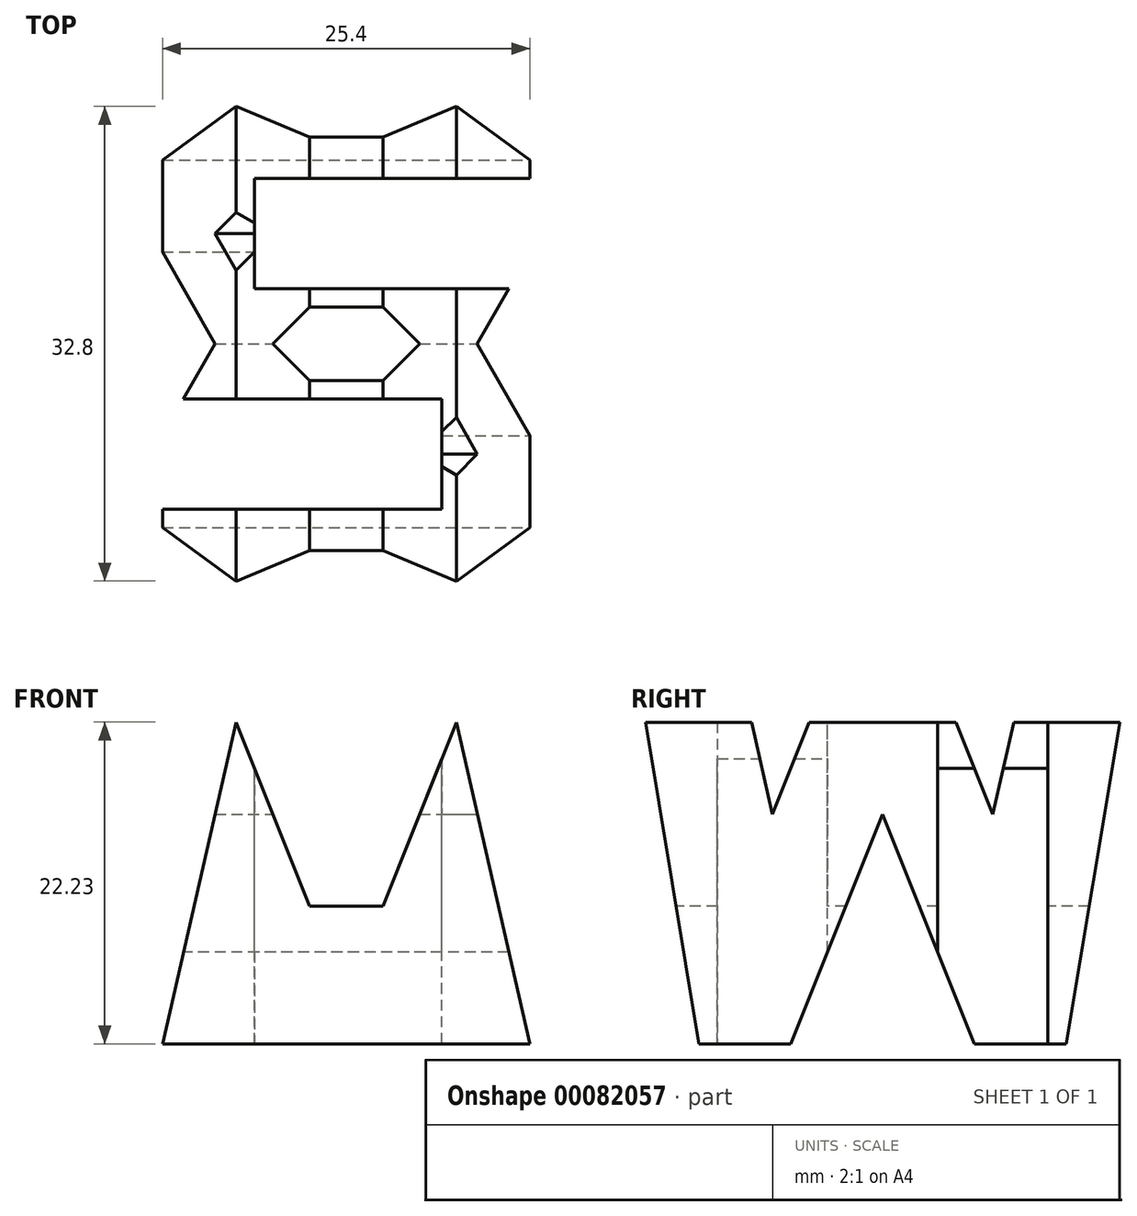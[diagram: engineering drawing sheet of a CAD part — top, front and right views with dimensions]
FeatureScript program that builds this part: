
annotation { "Feature Type Name" : "Feature", "Feature Type Description" : "" }
export const myFeature = defineFeature(function(context is Context, id is Id, definition is map)
    precondition{}
    {
        {
            var Q0;
            Q0=qCreatedBy(makeId("Front.planeOp"),FACE);
            var sketch = newSketch(context, id + "F0", { "sketchPlane" : qUnion([Q0])});
            skLineSegment(sketch, "E0", {"start": v(0, 0) * mm, "end": v(0, 38.1) * mm});
            skLineSegment(sketch, "E1", {"start": v(0, 38.1) * mm, "end": v(38.1, 38.1) * mm});
            skLineSegment(sketch, "E2", {"start": v(38.1, 38.1) * mm, "end": v(38.1, 0) * mm});
            skLineSegment(sketch, "E3", {"start": v(38.1, 0) * mm, "end": v(0, 0) * mm});
            skSolve(sketch);
        }
        {
            var Q0;
            Q0=makeQuery(id+"F0.imprint","IMPRINT",FACE,{"disambiguationData":[TD([[makeQuery(id+"F0.imprint","IMPRINT",EDGE,{"derivedFrom":sQuery(id+"F0.wireOp",EDGE,"E0")}),-1.0]])]});
            extrude(context, id + "F1", {"entities" : qUnion([Q0]), "depth" : 38.1 * mm});
        }
        {
            var Q0;
            Q0=qCreatedBy(makeId("Front.planeOp"),FACE);
            cPlane(context, id + "F2", {"entities" : qUnion([Q0]), "cplaneType" : CPlaneType.OFFSET, "offset" : 38.1 * mm, "width" : 152.4 * mm, "height" : 152.4 * mm});
        }
        {
            var Q0;
            Q0=qCreatedBy(makeId("Right.planeOp"),FACE);
            cPlane(context, id + "F3", {"entities" : qUnion([Q0]), "cplaneType" : CPlaneType.OFFSET, "offset" : 38.1 * mm, "width" : 152.4 * mm, "height" : 152.4 * mm});
        }
        {
            var Q0;
            Q0=qCreatedBy(makeId("Top.planeOp"),FACE);
            cPlane(context, id + "F4", {"entities" : qUnion([Q0]), "cplaneType" : CPlaneType.OFFSET, "offset" : 38.1 * mm, "width" : 152.4 * mm, "height" : 152.4 * mm});
        }
        {
            var Q0;
            Q0=qCreatedBy(id+"F3.planeOp",FACE);
            var sketch = newSketch(context, id + "F5", { "sketchPlane" : qUnion([Q0])});
            skLineSegment(sketch, "E4", {"start": v(0, 0) * mm, "end": v(0, 38.1) * mm});
            skLineSegment(sketch, "E5", {"start": v(0, 38.1) * mm, "end": v(-38.1, 38.1) * mm});
            skLineSegment(sketch, "E6", {"start": v(-38.1, 38.1) * mm, "end": v(-38.1, 0) * mm});
            skLineSegment(sketch, "E7", {"start": v(-38.1, 0) * mm, "end": v(0, 0) * mm});
            skLineSegment(sketch, "E8", {"start": v(-38.1, 38.1) * mm, "end": v(-31.75, 0) * mm});
            skLineSegment(sketch, "E9", {"start": v(-6.35, 0) * mm, "end": v(0, 38.1) * mm});
            skLineSegment(sketch, "E10", {"start": v(-6.35, 38.1) * mm, "end": v(-11.43, 15.87) * mm});
            skLineSegment(sketch, "E11", {"start": v(-16.5, 28.58) * mm, "end": v(-21.59, 28.58) * mm});
            skLineSegment(sketch, "E12", {"start": v(-21.59, 28.58) * mm, "end": v(-26.67, 15.87) * mm});
            skLineSegment(sketch, "E13", {"start": v(-26.67, 15.88) * mm, "end": v(-31.75, 38.1) * mm});
            skLineSegment(sketch, "E14", {"start": v(-16.5, 28.58) * mm, "end": v(-11.43, 15.88) * mm});
            skLineSegment(sketch, "E15", {"start": v(-25.4, 0) * mm, "end": v(-19.05, 15.88) * mm});
            skLineSegment(sketch, "E16", {"start": v(-19.05, 15.88) * mm, "end": v(-12.7, 0) * mm});
            skSolve(sketch);
        }
        {
            var Q0;
            {var subQ0=sQuery(id+"F5.wireOp",EDGE,"E10");Q0=makeQuery(id+"F5.imprint","IMPRINT",FACE,{"disambiguationData":[TD([[makeQuery(id+"F5.imprint","IMPRINT",EDGE,{"derivedFrom":subQ0}),-1.0]])]});}
            var Q1;
            {var subQ0=sQuery(id+"F5.wireOp",EDGE,"E6");Q1=makeQuery(id+"F5.imprint","IMPRINT",FACE,{"disambiguationData":[TD([[makeQuery(id+"F5.imprint","IMPRINT",EDGE,{"derivedFrom":subQ0}),1.0]])]});}
            var Q2;
            {var subQ0=sQuery(id+"F5.wireOp",EDGE,"E15");Q2=makeQuery(id+"F5.imprint","IMPRINT",FACE,{"disambiguationData":[TD([[makeQuery(id+"F5.imprint","IMPRINT",EDGE,{"derivedFrom":subQ0}),-1.0]])]});}
            var Q3;
            {var subQ0=sQuery(id+"F5.wireOp",EDGE,"E4");Q3=makeQuery(id+"F5.imprint","IMPRINT",FACE,{"disambiguationData":[TD([[makeQuery(id+"F5.imprint","IMPRINT",EDGE,{"derivedFrom":subQ0}),1.0]])]});}
            extrude(context, id + "F6", {"entities" : qUnion([Q0, Q1, Q2, Q3]), "operationType" : NewBodyOperationType.REMOVE, "oppositeDirection" : true, "depth" : 38.1 * mm});
        }
        {
            var Q0;
            Q0=qCreatedBy(id+"F2.planeOp",FACE);
            var sketch = newSketch(context, id + "F7", { "sketchPlane" : qUnion([Q0])});
            skLineSegment(sketch, "E17", {"start": v(0, 0) * mm, "end": v(0, 38.1) * mm});
            skLineSegment(sketch, "E18", {"start": v(0, 38.1) * mm, "end": v(38.1, 38.1) * mm});
            skLineSegment(sketch, "E19", {"start": v(38.1, 38.1) * mm, "end": v(38.1, 0) * mm});
            skLineSegment(sketch, "E20", {"start": v(38.1, 0) * mm, "end": v(0, 0) * mm});
            skLineSegment(sketch, "E21", {"start": v(11.43, 22.23) * mm, "end": v(16.51, 9.52) * mm});
            skLineSegment(sketch, "E22", {"start": v(16.51, 9.52) * mm, "end": v(21.59, 9.52) * mm});
            skLineSegment(sketch, "E23", {"start": v(21.59, 9.52) * mm, "end": v(26.67, 22.23) * mm});
            skLineSegment(sketch, "E24", {"start": v(11.43, 22.23) * mm, "end": v(6.35, 0) * mm});
            skLineSegment(sketch, "E25", {"start": v(26.67, 22.23) * mm, "end": v(31.75, 0) * mm});
            skLineSegment(sketch, "E26", {"start": v(31.75, 0) * mm, "end": v(38.1, 0) * mm});
            skLineSegment(sketch, "E27", {"start": v(31.75, 38.1) * mm, "end": v(38.1, 0) * mm});
            skLineSegment(sketch, "E28", {"start": v(25.4, 38.1) * mm, "end": v(19.05, 22.22) * mm});
            skLineSegment(sketch, "E29", {"start": v(19.05, 22.22) * mm, "end": v(12.7, 38.1) * mm});
            skLineSegment(sketch, "E30", {"start": v(12.7, 38.1) * mm, "end": v(6.35, 38.1) * mm});
            skLineSegment(sketch, "E31", {"start": v(6.35, 38.1) * mm, "end": v(0, 0) * mm});
            skLineSegment(sketch, "E32", {"start": v(6.35, 0) * mm, "end": v(0, 0) * mm});
            skSolve(sketch);
        }
        {
            var Q0;
            {var subQ0=sQuery(id+"F7.wireOp",EDGE,"E17");Q0=makeQuery(id+"F7.imprint","IMPRINT",FACE,{"disambiguationData":[TD([[makeQuery(id+"F7.imprint","IMPRINT",EDGE,{"derivedFrom":subQ0}),-1.0]])]});}
            var Q1;
            {var subQ0=sQuery(id+"F7.wireOp",EDGE,"E28");Q1=makeQuery(id+"F7.imprint","IMPRINT",FACE,{"disambiguationData":[TD([[makeQuery(id+"F7.imprint","IMPRINT",EDGE,{"derivedFrom":subQ0}),-1.0]])]});}
            var Q2;
            Q2=makeQuery(id+"F7.imprint","IMPRINT",FACE,{"disambiguationData":[TD([[makeQuery(id+"F7.imprint","IMPRINT",EDGE,{"derivedFrom":sQuery(id+"F7.wireOp",EDGE,"E20")}),-1.0]])]});
            var Q3;
            {var subQ0=sQuery(id+"F7.wireOp",EDGE,"E19");Q3=makeQuery(id+"F7.imprint","IMPRINT",FACE,{"disambiguationData":[TD([[makeQuery(id+"F7.imprint","IMPRINT",EDGE,{"derivedFrom":subQ0}),-1.0]])]});}
            extrude(context, id + "F8", {"entities" : qUnion([Q0, Q1, Q2, Q3]), "operationType" : NewBodyOperationType.REMOVE, "oppositeDirection" : true, "depth" : 38.1 * mm});
        }
        {
            var Q0;
            Q0=qCreatedBy(id+"F4.planeOp",FACE);
            var sketch = newSketch(context, id + "F9", { "sketchPlane" : qUnion([Q0])});
            skLineSegment(sketch, "E33", {"start": v(0, 0) * mm, "end": v(38.37, 0) * mm});
            skLineSegment(sketch, "E34", {"start": v(38.37, 0) * mm, "end": v(38.37, -38.1) * mm});
            skLineSegment(sketch, "E35", {"start": v(38.37, -38.1) * mm, "end": v(0, -38.1) * mm});
            skLineSegment(sketch, "E36", {"start": v(0, -38.1) * mm, "end": v(0, 0) * mm});
            skLineSegment(sketch, "E37", {"start": v(38.37, -7.62) * mm, "end": v(12.7, -7.62) * mm});
            skLineSegment(sketch, "E38", {"start": v(12.7, -7.62) * mm, "end": v(12.7, -15.24) * mm});
            skLineSegment(sketch, "E39", {"start": v(12.7, -15.24) * mm, "end": v(38.37, -15.24) * mm});
            skLineSegment(sketch, "E40", {"start": v(38.37, -15.24) * mm, "end": v(38.37, -7.62) * mm});
            skLineSegment(sketch, "E41", {"start": v(0, -22.86) * mm, "end": v(25.67, -22.86) * mm});
            skLineSegment(sketch, "E42", {"start": v(25.67, -22.86) * mm, "end": v(25.67, -30.48) * mm});
            skLineSegment(sketch, "E43", {"start": v(25.67, -30.48) * mm, "end": v(0, -30.48) * mm});
            skLineSegment(sketch, "E44", {"start": v(0, -30.48) * mm, "end": v(0, -22.86) * mm});
            skSolve(sketch);
        }
        {
            var Q0;
            Q0=makeQuery(id+"F9.imprint","IMPRINT",FACE,{"disambiguationData":[TD([[makeQuery(id+"F9.imprint","IMPRINT",EDGE,{"derivedFrom":sQuery(id+"F9.wireOp",EDGE,"E37")}),1.0]])]});
            var Q1;
            Q1=makeQuery(id+"F9.imprint","IMPRINT",FACE,{"disambiguationData":[TD([[makeQuery(id+"F9.imprint","IMPRINT",EDGE,{"derivedFrom":sQuery(id+"F9.wireOp",EDGE,"E41")}),-1.0]])]});
            extrude(context, id + "F10", {"entities" : qUnion([Q0, Q1]), "operationType" : NewBodyOperationType.REMOVE, "oppositeDirection" : true, "depth" : 38.1 * mm});
        }
    });
